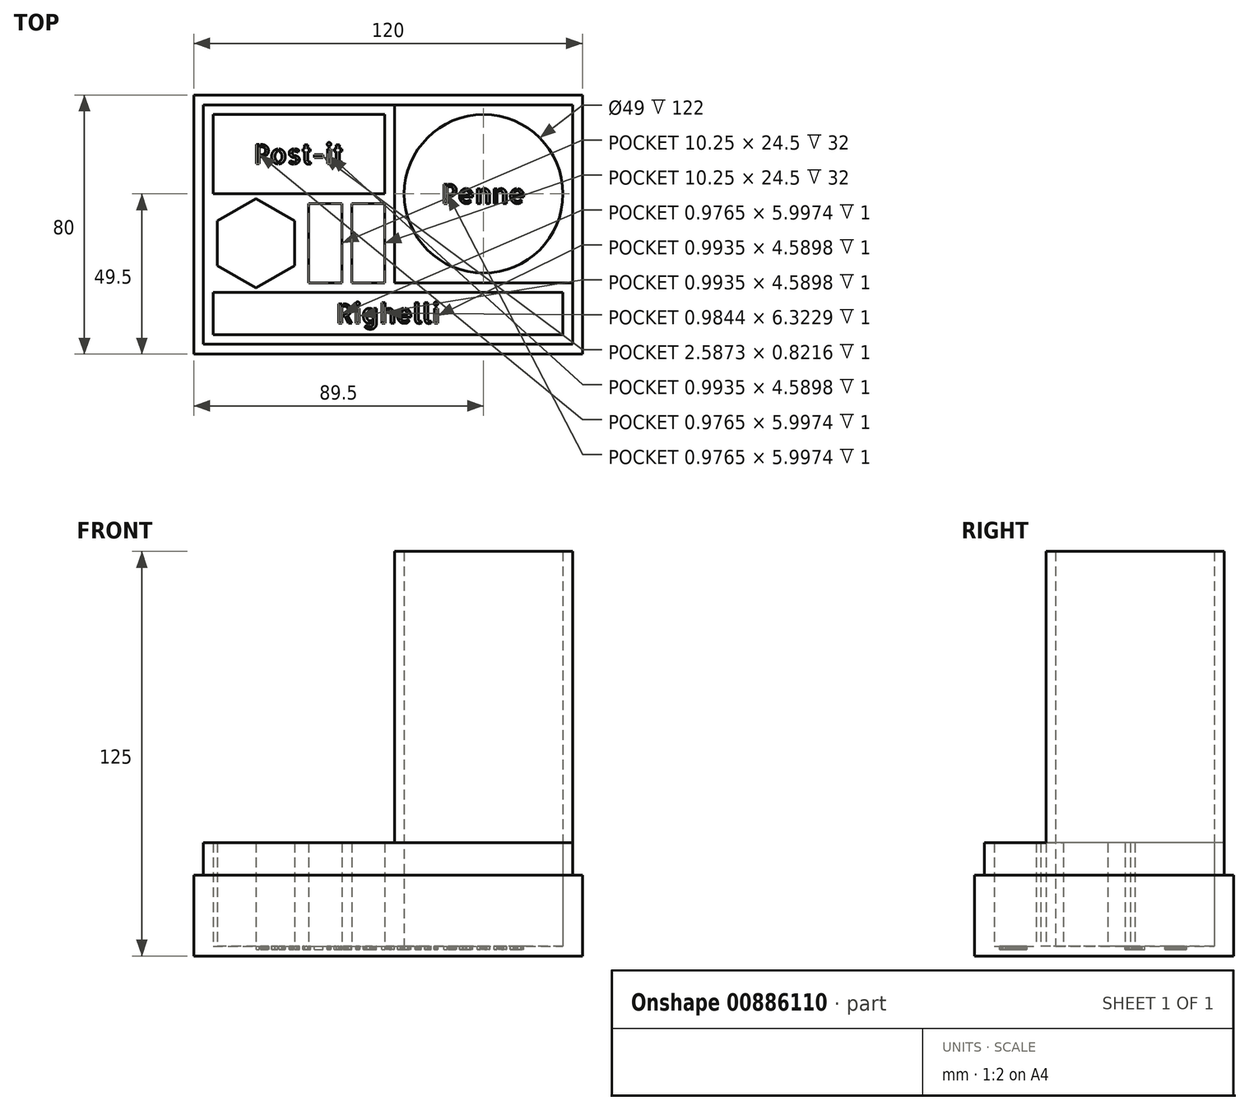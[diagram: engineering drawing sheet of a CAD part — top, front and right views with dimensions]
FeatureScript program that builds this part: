
annotation { "Feature Type Name" : "Feature", "Feature Type Description" : "" }
export const myFeature = defineFeature(function(context is Context, id is Id, definition is map)
    precondition{}
    {
        {
            var Q0;
            Q0=qCreatedBy(makeId("Top.planeOp"),FACE);
            var sketch = newSketch(context, id + "F0", { "sketchPlane" : qUnion([Q0])});
            skLineSegment(sketch, "E0.bottom", {"start": v(-60, 40) * mm, "end": v(60, 40) * mm});
            skLineSegment(sketch, "E0.top", {"start": v(-60, -40) * mm, "end": v(60, -40) * mm});
            skLineSegment(sketch, "E0.left", {"start": v(-60, 40) * mm, "end": v(-60, -40) * mm});
            skLineSegment(sketch, "E0.right", {"start": v(60, 40) * mm, "end": v(60, -40) * mm});
            skSolve(sketch);
        }
        {
            var Q0;
            Q0 = qSketchRegion(id + "F0", true);
            extrude(context, id + "F1", {"entities" : qUnion([Q0]), "depth" : 3 * mm, "offsetDistance" : 25 * mm});
        }
        {
            var Q0;
            Q0=makeQuery(id+"F1.opExtrude","CAP_FACE",FACE,{"disambiguationData":[OSD([sQuery(id+"F0.wireOp",EDGE,"E0.bottom"),sQuery(id+"F0.wireOp",EDGE,"E0.top"),sQuery(id+"F0.wireOp",EDGE,"E0.left"),sQuery(id+"F0.wireOp",EDGE,"E0.right")])],"isStart":false});
            var sketch = newSketch(context, id + "F2", { "sketchPlane" : qUnion([Q0])});
            skLineSegment(sketch, "E1.0.0", {"start": v(-60, 40) * mm, "end": v(-60, -40) * mm});
            skLineSegment(sketch, "E1.0.1", {"start": v(-60, -40) * mm, "end": v(60, -40) * mm});
            skLineSegment(sketch, "E1.0.2", {"start": v(60, -40) * mm, "end": v(60, 40) * mm});
            skLineSegment(sketch, "E1.0.3", {"start": v(60, 40) * mm, "end": v(-60, 40) * mm});
            skLineSegment(sketch, "E2.0", {"start": v(-57, 37) * mm, "end": v(-57, -37) * mm});
            skLineSegment(sketch, "E2.1", {"start": v(57, 37) * mm, "end": v(-57, 37) * mm});
            skLineSegment(sketch, "E2.2", {"start": v(57, -37) * mm, "end": v(57, 37) * mm});
            skLineSegment(sketch, "E2.3", {"start": v(-57, -37) * mm, "end": v(57, -37) * mm});
            skSolve(sketch);
        }
        {
            var Q0;
            Q0 = qSketchRegion(id + "F2", true);
            extrude(context, id + "F3", {"entities" : qUnion([Q0]), "operationType" : NewBodyOperationType.ADD, "depth" : 22 * mm, "offsetDistance" : 25 * mm});
        }
        {
            var Q0;
            Q0=makeQuery(id+"F1.opExtrude","CAP_FACE",FACE,{"disambiguationData":[OSD([sQuery(id+"F0.wireOp",EDGE,"E0.bottom"),sQuery(id+"F0.wireOp",EDGE,"E0.top"),sQuery(id+"F0.wireOp",EDGE,"E0.left"),sQuery(id+"F0.wireOp",EDGE,"E0.right")])],"isStart":false});
            var sketch = newSketch(context, id + "F4", { "sketchPlane" : qUnion([Q0])});
            skLineSegment(sketch, "E3.0.0", {"start": v(57, 37) * mm, "end": v(2, 37) * mm});
            skLineSegment(sketch, "E3.0.1", {"start": v(2, 37) * mm, "end": v(2, -18) * mm});
            skLineSegment(sketch, "E3.0.2", {"start": v(2, -18) * mm, "end": v(57, -18) * mm});
            skLineSegment(sketch, "E3.0.3", {"start": v(57, -18) * mm, "end": v(57, 37) * mm});
            skCircle(sketch, "E4", {"center": v(29.5, 9.5) * mm, "radius": 24.5 * mm});
            skPoint(sketch, "E4.centerSnap0", {"position": v(2, 9.5) * mm});
            skPoint(sketch, "E4.centerSnap1", {"position": v(29.5, -18) * mm});
            skLineSegment(sketch, "E5.0.0", {"start": v(-57, 37) * mm, "end": v(-57, -37) * mm, "construction": true});
            skLineSegment(sketch, "E5.0.1", {"start": v(-57, -37) * mm, "end": v(57, -37) * mm, "construction": true});
            skLineSegment(sketch, "E5.0.2", {"start": v(57, -37) * mm, "end": v(57, 37) * mm, "construction": true});
            skLineSegment(sketch, "E5.0.3", {"start": v(57, 37) * mm, "end": v(-57, 37) * mm, "construction": true});
            skSolve(sketch);
        }
        {
            var Q0;
            Q0 = qSketchRegion(id + "F4", true);
            extrude(context, id + "F5", {"entities" : qUnion([Q0]), "operationType" : NewBodyOperationType.ADD, "depth" : 122 * mm, "offsetDistance" : 25 * mm});
        }
        {
            var Q0;
            Q0=makeQuery(id+"F1.opExtrude","CAP_FACE",FACE,{"disambiguationData":[OSD([sQuery(id+"F0.wireOp",EDGE,"E0.bottom"),sQuery(id+"F0.wireOp",EDGE,"E0.top"),sQuery(id+"F0.wireOp",EDGE,"E0.left"),sQuery(id+"F0.wireOp",EDGE,"E0.right")])],"isStart":false});
            var sketch = newSketch(context, id + "F6", { "sketchPlane" : qUnion([Q0])});
            skLineSegment(sketch, "E6.0.0", {"start": v(57, -37) * mm, "end": v(57, -18) * mm, "construction": true});
            skLineSegment(sketch, "E6.0.1", {"start": v(57, -18) * mm, "end": v(2, -18) * mm, "construction": true});
            skLineSegment(sketch, "E6.0.2", {"start": v(2, -18) * mm, "end": v(2, 37) * mm, "construction": true});
            skLineSegment(sketch, "E6.0.3", {"start": v(2, 37) * mm, "end": v(-57, 37) * mm, "construction": true});
            skLineSegment(sketch, "E6.0.4", {"start": v(-57, 37) * mm, "end": v(-57, -37) * mm, "construction": true});
            skLineSegment(sketch, "E6.0.5", {"start": v(-57, -37) * mm, "end": v(57, -37) * mm, "construction": true});
            skLineSegment(sketch, "E7.bottom", {"start": v(-57, 37) * mm, "end": v(2, 37) * mm});
            skLineSegment(sketch, "E7.left", {"start": v(-57, 37) * mm, "end": v(-57, -18) * mm});
            skLineSegment(sketch, "E7.right", {"start": v(2, 37) * mm, "end": v(2, -18) * mm});
            skLineSegment(sketch, "E8.0", {"start": v(-1, 9.5) * mm, "end": v(-1, 34) * mm});
            skLineSegment(sketch, "E9.0", {"start": v(-1, 34) * mm, "end": v(-54, 34) * mm});
            skLineSegment(sketch, "E10.0", {"start": v(-54, 34) * mm, "end": v(-54, 9.5) * mm});
            skLineSegment(sketch, "E11", {"start": v(-54, 9.5) * mm, "end": v(-1, 9.5) * mm});
            skPoint(sketch, "E12.startSnap0", {"position": v(-27.5, 9.5) * mm});
            skLineSegment(sketch, "E13.bottom", {"start": v(-24.5, 6.5) * mm, "end": v(-14.25, 6.5) * mm});
            skLineSegment(sketch, "E13.top", {"start": v(-24.5, -18) * mm, "end": v(-14.25, -18) * mm});
            skLineSegment(sketch, "E13.left", {"start": v(-24.5, 6.5) * mm, "end": v(-24.5, -18) * mm});
            skLineSegment(sketch, "E13.right", {"start": v(-14.25, 6.5) * mm, "end": v(-14.25, -18) * mm});
            skLineSegment(sketch, "E14.bottom", {"start": v(-11.25, 6.5) * mm, "end": v(-1, 6.5) * mm});
            skLineSegment(sketch, "E14.top", {"start": v(-11.25, -18) * mm, "end": v(-1, -18) * mm});
            skLineSegment(sketch, "E14.left", {"start": v(-11.25, 6.5) * mm, "end": v(-11.25, -18) * mm});
            skLineSegment(sketch, "E14.right", {"start": v(-1, 6.5) * mm, "end": v(-1, -18) * mm});
            skLineSegment(sketch, "E15.bottom", {"start": v(2, -18) * mm, "end": v(57, -18) * mm});
            skLineSegment(sketch, "E15.top", {"start": v(-57, -37) * mm, "end": v(57, -37) * mm});
            skLineSegment(sketch, "E15.left", {"start": v(-57, -18) * mm, "end": v(-57, -37) * mm});
            skLineSegment(sketch, "E15.right", {"start": v(57, -18) * mm, "end": v(57, -37) * mm});
            skLineSegment(sketch, "E16.0", {"start": v(-54, -21) * mm, "end": v(54, -21) * mm});
            skLineSegment(sketch, "E17.0", {"start": v(-54, 37) * mm, "end": v(-54, 9.5) * mm});
            skLineSegment(sketch, "E18.0", {"start": v(-54, -34) * mm, "end": v(54, -34) * mm});
            skLineSegment(sketch, "E19.0", {"start": v(54, -34) * mm, "end": v(54, -21) * mm});
            skLineSegment(sketch, "E20.trimOffspring", {"start": v(-54, -21) * mm, "end": v(-54, -34) * mm});
            skCircle(sketch, "E21.cCircle", {"center": v(-40.75, -5.75) * mm, "radius": 11.96 * mm, "construction": true});
            skLineSegment(sketch, "E21.0", {"start": v(-28.79, 1.16) * mm, "end": v(-28.79, -12.66) * mm});
            skLineSegment(sketch, "E21.1", {"start": v(-28.79, -12.66) * mm, "end": v(-40.75, -19.56) * mm});
            skLineSegment(sketch, "E21.2", {"start": v(-40.75, -19.56) * mm, "end": v(-52.71, -12.66) * mm});
            skLineSegment(sketch, "E21.3", {"start": v(-52.71, -12.66) * mm, "end": v(-52.71, 1.16) * mm});
            skLineSegment(sketch, "E21.4", {"start": v(-52.71, 1.16) * mm, "end": v(-40.75, 8.06) * mm});
            skLineSegment(sketch, "E21.5", {"start": v(-40.75, 8.06) * mm, "end": v(-28.79, 1.16) * mm});
            skPoint(sketch, "E21.0.midPoint", {"position": v(-28.79, -5.75) * mm});
            skSolve(sketch);
        }
        {
            var Q0;
            Q0 = qSketchRegion(id + "F6", true);
            extrude(context, id + "F7", {"entities" : qUnion([Q0]), "operationType" : NewBodyOperationType.ADD, "depth" : 32 * mm, "offsetDistance" : 25 * mm});
        }
        {
            var Q0;
            Q0=makeQuery(id+"F7.boolean.opBoolean","SPLIT",FACE,{"disambiguationData":[TD([makeQuery(id+"F7.opExtrude","SWEPT_FACE",FACE,{"disambiguationData":[OSD([sQuery(id+"F6.wireOp",EDGE,"E8.0")])]})])],"derivedFrom":makeQuery(id+"F1.opExtrude","CAP_FACE",FACE,{"disambiguationData":[OSD([sQuery(id+"F0.wireOp",EDGE,"E0.bottom"),sQuery(id+"F0.wireOp",EDGE,"E0.top"),sQuery(id+"F0.wireOp",EDGE,"E0.left"),sQuery(id+"F0.wireOp",EDGE,"E0.right")])],"isStart":false})});
            var sketch = newSketch(context, id + "F8", { "sketchPlane" : qUnion([Q0])});
            skLineSegment(sketch, "E22.0.0", {"start": v(-54, 34) * mm, "end": v(-54, 9.5) * mm, "construction": true});
            skLineSegment(sketch, "E22.0.1", {"start": v(-54, 9.5) * mm, "end": v(-1, 9.5) * mm, "construction": true});
            skLineSegment(sketch, "E22.0.2", {"start": v(-1, 9.5) * mm, "end": v(-1, 34) * mm, "construction": true});
            skLineSegment(sketch, "E22.0.3", {"start": v(-1, 34) * mm, "end": v(-54, 34) * mm, "construction": true});
            skText(sketch, "E23", { "text": "Post-it", "fontName": "AllertaStencil-Regular.ttf"});
            skLineSegment(sketch, "E24", {"start": v(-27.5, 24.75) * mm, "end": v(-27.5, 34) * mm, "construction": true});
            skLineSegment(sketch, "E25", {"start": v(-27.5, 18.75) * mm, "end": v(-27.5, 9.5) * mm, "construction": true});
            skLineSegment(sketch, "E26", {"start": v(-41.46, 24.75) * mm, "end": v(-54, 24.75) * mm, "construction": true});
            skLineSegment(sketch, "E27", {"start": v(-13.54, 24.75) * mm, "end": v(-1, 24.75) * mm, "construction": true});
            skLineSegment(sketch, "E28.0.0", {"start": v(-54, -34) * mm, "end": v(54, -34) * mm, "construction": true});
            skLineSegment(sketch, "E28.0.1", {"start": v(54, -34) * mm, "end": v(54, -21) * mm, "construction": true});
            skLineSegment(sketch, "E28.0.2", {"start": v(54, -21) * mm, "end": v(-54, -21) * mm, "construction": true});
            skLineSegment(sketch, "E28.0.3", {"start": v(-54, -21) * mm, "end": v(-54, -34) * mm, "construction": true});
            skText(sketch, "E29", { "text": "Righelli", "fontName": "AllertaStencil-Regular.ttf"});
            skLineSegment(sketch, "E30", {"start": v(0, -24.5) * mm, "end": v(0, -21) * mm, "construction": true});
            skLineSegment(sketch, "E31", {"start": v(0, -30.5) * mm, "end": v(0, -34) * mm, "construction": true});
            skLineSegment(sketch, "E32", {"start": v(15.95, -24.5) * mm, "end": v(54, -24.5) * mm, "construction": true});
            skLineSegment(sketch, "E33", {"start": v(-15.95, -24.5) * mm, "end": v(-54, -24.5) * mm, "construction": true});
            skCircle(sketch, "E34.0", {"center": v(29.5, 9.5) * mm, "radius": 24.5 * mm, "construction": true});
            skText(sketch, "E35", { "text": "Penne", "fontName": "AllertaStencil-Regular.ttf"});
            const initialGuessF8  = {"E23": [-0.04146, 0.01875, 1, 0, 0.006], "E29": [-0.01595, -0.0305, 1, 0, 0.006], "E35": [0.01652, 0.0065, 1, 0, 0.006]};
            skSetInitialGuess(sketch, initialGuessF8);
            skSolve(sketch);
        }
        {
            var Q0;
            Q0 = qSketchRegion(id + "F8", true);
            extrude(context, id + "F9", {"entities" : qUnion([Q0]), "operationType" : NewBodyOperationType.REMOVE, "oppositeDirection" : true, "depth" : 1 * mm, "offsetDistance" : 25 * mm});
        }
    });
